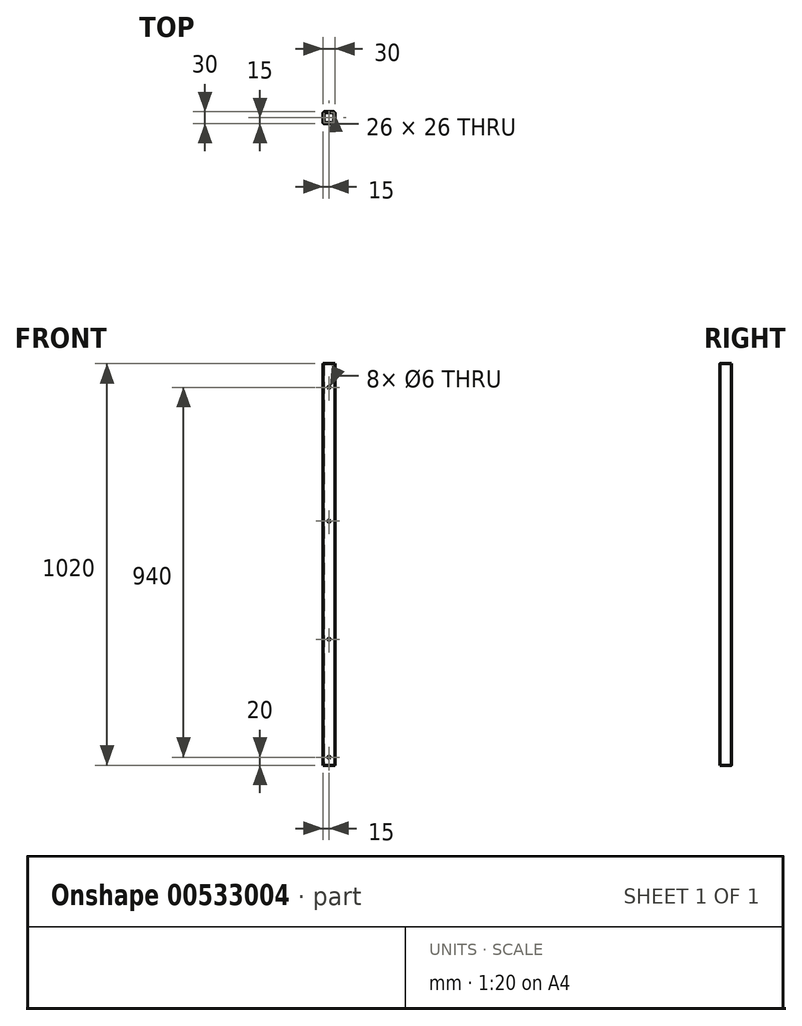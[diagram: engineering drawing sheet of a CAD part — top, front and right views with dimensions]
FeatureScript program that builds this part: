
annotation { "Feature Type Name" : "Feature", "Feature Type Description" : "" }
export const myFeature = defineFeature(function(context is Context, id is Id, definition is map)
    precondition{}
    {
        {
            var Q0;
            Q0=qCreatedBy(makeId("Top.planeOp"),FACE);
            var sketch = newSketch(context, id + "F0", { "sketchPlane" : qUnion([Q0])});
            skLineSegment(sketch, "E0.bottom", {"start": v(11.5, 15) * mm, "end": v(-11.5, 15) * mm});
            skLineSegment(sketch, "E0.top", {"start": v(11.5, -15) * mm, "end": v(-11.5, -15) * mm});
            skLineSegment(sketch, "E0.left", {"start": v(15, 11.5) * mm, "end": v(15, -11.5) * mm});
            skLineSegment(sketch, "E0.right", {"start": v(-15, 11.5) * mm, "end": v(-15, -11.5) * mm});
            skPoint(sketch, "E0.middle", {"position": v(0, 0) * mm});
            skLineSegment(sketch, "E1.bottom", {"start": v(13, -13) * mm, "end": v(-13, -13) * mm});
            skLineSegment(sketch, "E1.top", {"start": v(13, 13) * mm, "end": v(-13, 13) * mm});
            skLineSegment(sketch, "E1.left", {"start": v(13, -13) * mm, "end": v(13, 13) * mm});
            skLineSegment(sketch, "E1.right", {"start": v(-13, -13) * mm, "end": v(-13, 13) * mm});
            skPoint(sketch, "E2.visualSharp", {"position": v(-15, 15) * mm});
            skArc(sketch, "E2.filletArc", {"start": v(-11.5, 15) * mm, "mid": v(-13.97, 13.97) * mm, "end": v(-15, 11.5) * mm});
            skPoint(sketch, "E3.visualSharp", {"position": v(-15, -15) * mm});
            skArc(sketch, "E3.filletArc", {"start": v(-15, -11.5) * mm, "mid": v(-13.97, -13.97) * mm, "end": v(-11.5, -15) * mm});
            skPoint(sketch, "E4.visualSharp", {"position": v(15, -15) * mm});
            skArc(sketch, "E4.filletArc", {"start": v(11.5, -15) * mm, "mid": v(13.97, -13.97) * mm, "end": v(15, -11.5) * mm});
            skPoint(sketch, "E5.visualSharp", {"position": v(15, 15) * mm});
            skArc(sketch, "E5.filletArc", {"start": v(15, 11.5) * mm, "mid": v(13.97, 13.97) * mm, "end": v(11.5, 15) * mm});
            skSolve(sketch);
        }
        {
            var Q0;
            Q0=makeQuery(id+"F0.imprint","IMPRINT",FACE,{"disambiguationData":[TD([[makeQuery(id+"F0.imprint","IMPRINT",EDGE,{"derivedFrom":sQuery(id+"F0.wireOp",EDGE,"E0.bottom")}),1.0]])]});
            extrude(context, id + "F1", {"entities" : qUnion([Q0]), "depth" : 1020 * mm, "offsetDistance" : 25 * mm});
        }
        {
            var Q0;
            Q0=makeQuery(id+"F1.opExtrude","SWEPT_FACE",FACE,{"disambiguationData":[OSD([sQuery(id+"F0.wireOp",EDGE,"E0.top")])]});
            var sketch = newSketch(context, id + "F2", { "sketchPlane" : qUnion([Q0])});
            skPoint(sketch, "E6", {"position": v(0, 20) * mm});
            skPoint(sketch, "E7", {"position": v(0, 320) * mm});
            skPoint(sketch, "E8", {"position": v(0, 620) * mm});
            skPoint(sketch, "E9", {"position": v(0, 960) * mm});
            skSolve(sketch);
        }
        {
            var Q0;
            Q0=sQuery(id+"F2.wireOp",VERTEX,"E9");
            var Q1;
            Q1=sQuery(id+"F2.wireOp",VERTEX,"E8");
            var Q2;
            Q2=sQuery(id+"F2.wireOp",VERTEX,"E7");
            var Q3;
            Q3=sQuery(id+"F2.wireOp",VERTEX,"E6");
            var Q4;
            Q4=makeQuery(id+"F1.opExtrude","SWEPT_BODY",BODY,{"disambiguationData":[OSD([sQuery(id+"F0.wireOp",EDGE,"E0.bottom"),sQuery(id+"F0.wireOp",EDGE,"E0.top"),sQuery(id+"F0.wireOp",EDGE,"E0.left"),sQuery(id+"F0.wireOp",EDGE,"E0.right"),sQuery(id+"F0.wireOp",EDGE,"E1.bottom"),sQuery(id+"F0.wireOp",EDGE,"E1.top"),sQuery(id+"F0.wireOp",EDGE,"E1.left"),sQuery(id+"F0.wireOp",EDGE,"E1.right"),sQuery(id+"F0.wireOp",EDGE,"E2.filletArc"),sQuery(id+"F0.wireOp",EDGE,"E3.filletArc"),sQuery(id+"F0.wireOp",EDGE,"E4.filletArc"),sQuery(id+"F0.wireOp",EDGE,"E5.filletArc")])]});
            hole(context, id + "F3", {"style" : HoleStyle.SIMPLE, "endStyle" : HoleEndStyle.THROUGH, "holeDiameter" : 6 * mm, "majorDiameter" : 5 * mm, "isTappedThrough" : true, "tappedDepth" : 12 * mm, "tapClearance" : 3, "locations" : qUnion([Q0, Q1, Q2, Q3]), "scope" : qUnion([Q4])});
        }
    });
